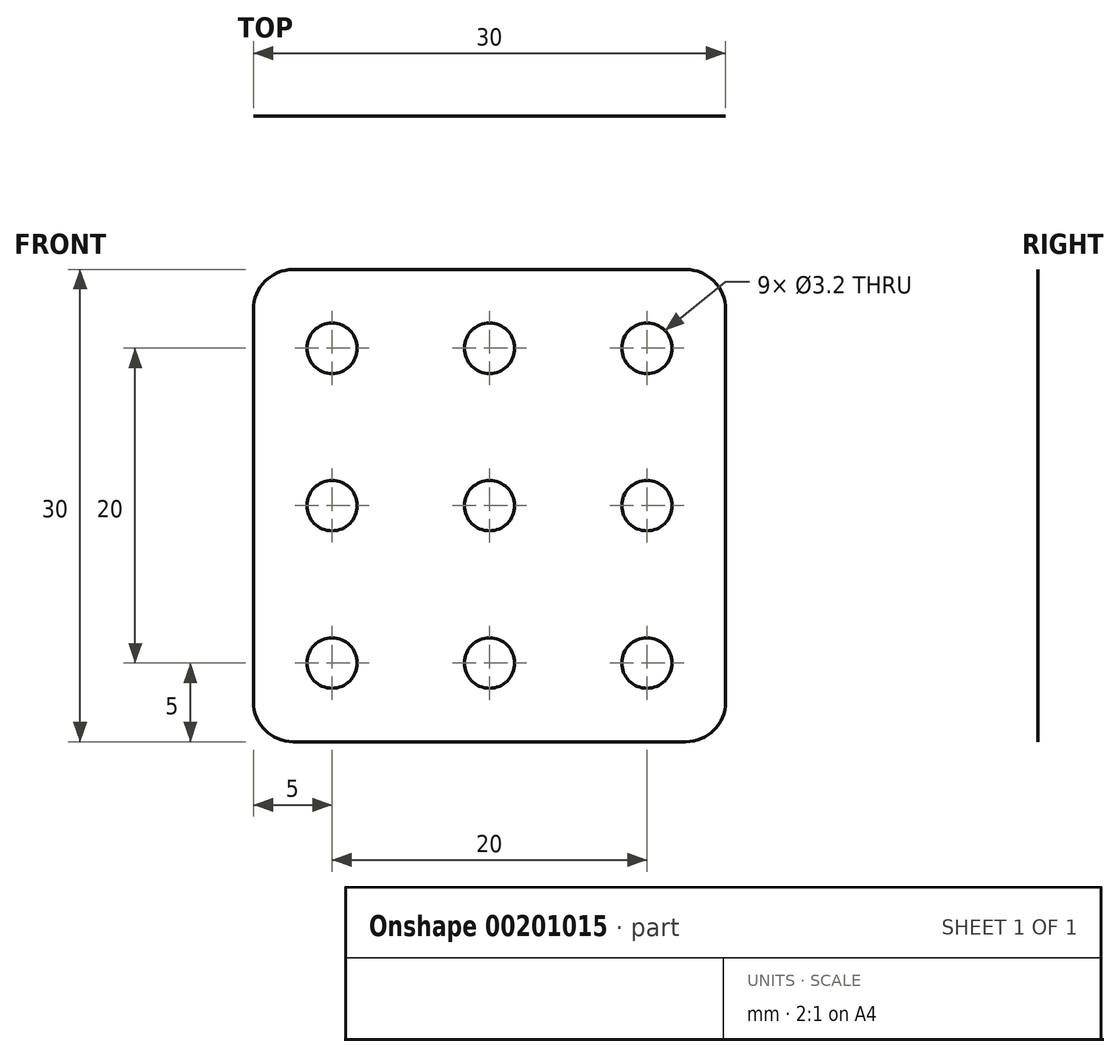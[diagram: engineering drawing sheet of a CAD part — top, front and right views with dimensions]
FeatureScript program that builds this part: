
annotation { "Feature Type Name" : "Feature", "Feature Type Description" : "" }
export const myFeature = defineFeature(function(context is Context, id is Id, definition is map)
    precondition{}
    {
        {
            var Q0;
            Q0=qCreatedBy(makeId("Front.planeOp"),FACE);
            var sketch = newSketch(context, id + "F0", { "sketchPlane" : qUnion([Q0])});
            skLineSegment(sketch, "E0.bottom", {"start": v(2.54, 0) * mm, "end": v(27.46, 0) * mm});
            skLineSegment(sketch, "E0.top", {"start": v(2.54, -30) * mm, "end": v(27.46, -30) * mm});
            skLineSegment(sketch, "E0.left", {"start": v(0, -2.54) * mm, "end": v(0, -27.46) * mm});
            skLineSegment(sketch, "E0.right", {"start": v(30, -2.54) * mm, "end": v(30, -27.46) * mm});
            skPoint(sketch, "E1.visualSharp", {"position": v(0, 0) * mm});
            skArc(sketch, "E1.filletArc", {"start": v(2.54, 0) * mm, "mid": v(0.74, -0.74) * mm, "end": v(0, -2.54) * mm});
            skPoint(sketch, "E2.visualSharp", {"position": v(30, 0) * mm});
            skArc(sketch, "E2.filletArc", {"start": v(30, -2.54) * mm, "mid": v(29.26, -0.74) * mm, "end": v(27.46, 0) * mm});
            skPoint(sketch, "E3.visualSharp", {"position": v(30, -30) * mm});
            skArc(sketch, "E3.filletArc", {"start": v(27.46, -30) * mm, "mid": v(29.26, -29.26) * mm, "end": v(30, -27.46) * mm});
            skPoint(sketch, "E4.visualSharp", {"position": v(0, -30) * mm});
            skArc(sketch, "E4.filletArc", {"start": v(0, -27.46) * mm, "mid": v(0.74, -29.26) * mm, "end": v(2.54, -30) * mm});
            skCircle(sketch, "E5", {"center": v(5, -5) * mm, "radius": 1.6 * mm});
            skCircle(sketch, "E6.0.1.0", {"center": v(5, -15) * mm, "radius": 1.6 * mm});
            skCircle(sketch, "E6.0.2.0", {"center": v(5, -25) * mm, "radius": 1.6 * mm});
            skCircle(sketch, "E6.1.0.0", {"center": v(15, -5) * mm, "radius": 1.6 * mm});
            skCircle(sketch, "E6.1.1.0", {"center": v(15, -15) * mm, "radius": 1.6 * mm});
            skCircle(sketch, "E6.1.2.0", {"center": v(15, -25) * mm, "radius": 1.6 * mm});
            skCircle(sketch, "E6.2.0.0", {"center": v(25, -5) * mm, "radius": 1.6 * mm});
            skCircle(sketch, "E6.2.1.0", {"center": v(25, -15) * mm, "radius": 1.6 * mm});
            skCircle(sketch, "E6.2.2.0", {"center": v(25, -25) * mm, "radius": 1.6 * mm});
            skLineSegment(sketch, "E6.direction1", {"start": v(5, -5) * mm, "end": v(15, -5) * mm, "construction": true});
            skLineSegment(sketch, "E6.direction2", {"start": v(5, -5) * mm, "end": v(5, -15) * mm, "construction": true});
            skSolve(sketch);
        }
        {
            var Q0;
            Q0=makeQuery(id+"F0.imprint","IMPRINT",FACE,{"disambiguationData":[TD([[makeQuery(id+"F0.imprint","IMPRINT",EDGE,{"derivedFrom":sQuery(id+"F0.wireOp",EDGE,"E0.bottom")}),-1.0]])]});
            extrude(context, id + "F1", {"entities" : qUnion([Q0]), "depth" : 1 / 203.2 * mm});
        }
    });
